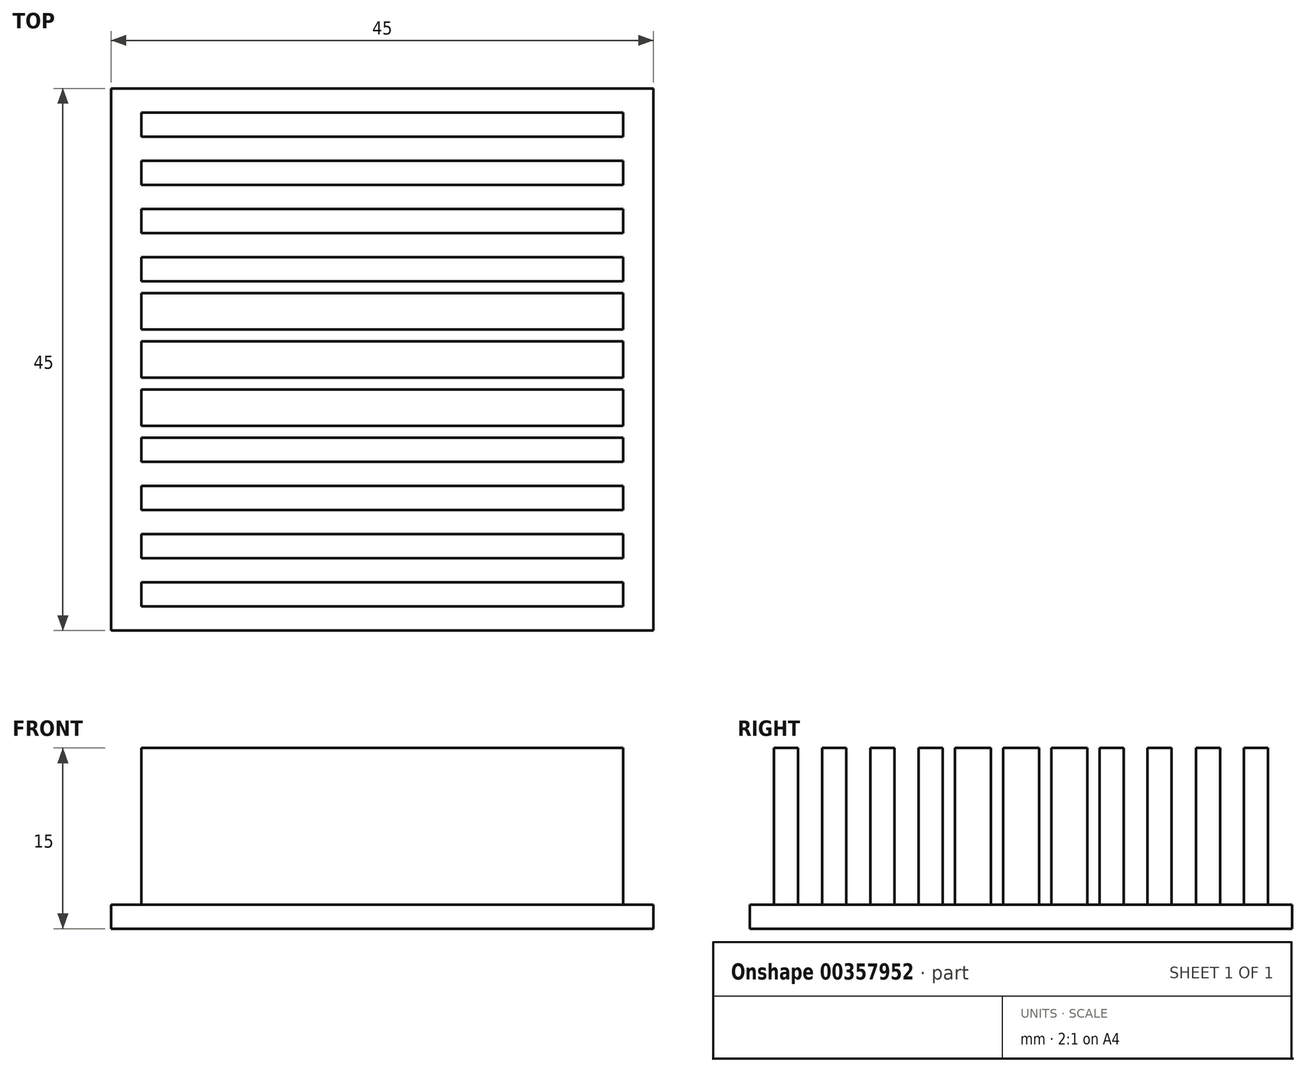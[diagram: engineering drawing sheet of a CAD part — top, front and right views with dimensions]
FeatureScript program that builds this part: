
annotation { "Feature Type Name" : "Feature", "Feature Type Description" : "" }
export const myFeature = defineFeature(function(context is Context, id is Id, definition is map)
    precondition{}
    {
        {
            var Q0;
            Q0=qCreatedBy(makeId("Top.planeOp"),FACE);
            var sketch = newSketch(context, id + "F0", { "sketchPlane" : qUnion([Q0])});
            skLineSegment(sketch, "E0.bottom", {"start": v(-22.5, 22.5) * mm, "end": v(22.5, 22.5) * mm});
            skLineSegment(sketch, "E0.top", {"start": v(-22.5, -22.5) * mm, "end": v(22.5, -22.5) * mm});
            skLineSegment(sketch, "E0.left", {"start": v(-22.5, 22.5) * mm, "end": v(-22.5, -22.5) * mm});
            skLineSegment(sketch, "E0.right", {"start": v(22.5, 22.5) * mm, "end": v(22.5, -22.5) * mm});
            skSolve(sketch);
        }
        {
            var Q0;
            Q0=qSketchRegion(id+"F0",true);
            extrude(context, id + "F1", {"entities" : qUnion([Q0]), "depth" : 15 * mm});
        }
        {
            var Q0;
            Q0=makeQuery(id+"F1.opExtrude","CAP_FACE",FACE,{"disambiguationData":[OSD([sQuery(id+"F0.wireOp",EDGE,"E0.bottom"),sQuery(id+"F0.wireOp",EDGE,"E0.top"),sQuery(id+"F0.wireOp",EDGE,"E0.left"),sQuery(id+"F0.wireOp",EDGE,"E0.right")])],"isStart":false});
            var sketch = newSketch(context, id + "F2", { "sketchPlane" : qUnion([Q0])});
            skLineSegment(sketch, "E1", {"start": v(-22.5, 22.5) * mm, "end": v(22.5, 22.5) * mm});
            skLineSegment(sketch, "E2", {"start": v(22.5, 22.5) * mm, "end": v(22.5, -22.5) * mm});
            skLineSegment(sketch, "E3", {"start": v(22.5, -22.5) * mm, "end": v(-22.5, -22.5) * mm});
            skLineSegment(sketch, "E4", {"start": v(-22.5, -22.5) * mm, "end": v(-22.5, 22.5) * mm});
            skLineSegment(sketch, "E5.bottom", {"start": v(-20, 20.5) * mm, "end": v(20, 20.5) * mm});
            skLineSegment(sketch, "E5.top", {"start": v(-20, 18.5) * mm, "end": v(20, 18.5) * mm});
            skLineSegment(sketch, "E5.left", {"start": v(-20, 20.5) * mm, "end": v(-20, 18.5) * mm});
            skLineSegment(sketch, "E5.right", {"start": v(20, 20.5) * mm, "end": v(20, 18.5) * mm});
            skLineSegment(sketch, "E6.bottom", {"start": v(-20, 16.5) * mm, "end": v(20, 16.5) * mm});
            skLineSegment(sketch, "E6.top", {"start": v(-20, 14.5) * mm, "end": v(20, 14.5) * mm});
            skLineSegment(sketch, "E6.left", {"start": v(-20, 16.5) * mm, "end": v(-20, 14.5) * mm});
            skLineSegment(sketch, "E6.right", {"start": v(20, 16.5) * mm, "end": v(20, 14.5) * mm});
            skLineSegment(sketch, "E7.bottom", {"start": v(-20, 12.5) * mm, "end": v(20, 12.5) * mm});
            skLineSegment(sketch, "E7.top", {"start": v(-20, 10.5) * mm, "end": v(20, 10.5) * mm});
            skLineSegment(sketch, "E7.left", {"start": v(-20, 12.5) * mm, "end": v(-20, 10.5) * mm});
            skLineSegment(sketch, "E7.right", {"start": v(20, 12.5) * mm, "end": v(20, 10.5) * mm});
            skLineSegment(sketch, "E8.bottom", {"start": v(-20, 8.5) * mm, "end": v(20, 8.5) * mm});
            skLineSegment(sketch, "E8.top", {"start": v(-20, 6.5) * mm, "end": v(20, 6.5) * mm});
            skLineSegment(sketch, "E8.left", {"start": v(-20, 8.5) * mm, "end": v(-20, 6.5) * mm});
            skLineSegment(sketch, "E8.right", {"start": v(20, 8.5) * mm, "end": v(20, 6.5) * mm});
            skLineSegment(sketch, "E9.bottom", {"start": v(-20, 4.5) * mm, "end": v(20, 4.5) * mm});
            skLineSegment(sketch, "E9.top", {"start": v(-20, 2.5) * mm, "end": v(20, 2.5) * mm});
            skLineSegment(sketch, "E9.left", {"start": v(-20, 4.5) * mm, "end": v(-20, 2.5) * mm});
            skLineSegment(sketch, "E9.right", {"start": v(20, 4.5) * mm, "end": v(20, 2.5) * mm});
            skLineSegment(sketch, "E10.bottom", {"start": v(-20, 0.5) * mm, "end": v(20, 0.5) * mm});
            skLineSegment(sketch, "E10.top", {"start": v(-20, -1.5) * mm, "end": v(20, -1.5) * mm});
            skLineSegment(sketch, "E10.left", {"start": v(-20, 0.5) * mm, "end": v(-20, -1.5) * mm});
            skLineSegment(sketch, "E10.right", {"start": v(20, 0.5) * mm, "end": v(20, -1.5) * mm});
            skLineSegment(sketch, "E11.bottom", {"start": v(-20, -3.5) * mm, "end": v(20, -3.5) * mm});
            skLineSegment(sketch, "E11.top", {"start": v(-20, -5.5) * mm, "end": v(20, -5.5) * mm});
            skLineSegment(sketch, "E11.left", {"start": v(-20, -3.5) * mm, "end": v(-20, -5.5) * mm});
            skLineSegment(sketch, "E11.right", {"start": v(20, -3.5) * mm, "end": v(20, -5.5) * mm});
            skLineSegment(sketch, "E12.MirrorCS", {"start": v(-20, -12.5) * mm, "end": v(-20, -10.5) * mm});
            skLineSegment(sketch, "E13.MirrorCS", {"start": v(20, -12.5) * mm, "end": v(20, -10.5) * mm});
            skLineSegment(sketch, "E14.MirrorCS", {"start": v(20, -0.5) * mm, "end": v(20, 1.5) * mm});
            skLineSegment(sketch, "E15.MirrorCS", {"start": v(20, -4.5) * mm, "end": v(20, -2.5) * mm});
            skLineSegment(sketch, "E16.MirrorCS", {"start": v(-20, -20.5) * mm, "end": v(-20, -18.5) * mm});
            skLineSegment(sketch, "E17.MirrorCS", {"start": v(20, -20.5) * mm, "end": v(20, -18.5) * mm});
            skLineSegment(sketch, "E18.MirrorCS", {"start": v(-20, -16.5) * mm, "end": v(-20, -14.5) * mm});
            skLineSegment(sketch, "E19.MirrorCS", {"start": v(20, -16.5) * mm, "end": v(20, -14.5) * mm});
            skLineSegment(sketch, "E20.MirrorCS", {"start": v(20, -8.5) * mm, "end": v(20, -6.5) * mm});
            skLineSegment(sketch, "E21.MirrorCS", {"start": v(-20, -0.5) * mm, "end": v(-20, 1.5) * mm});
            skLineSegment(sketch, "E22.MirrorCS", {"start": v(-20, -4.5) * mm, "end": v(-20, -2.5) * mm});
            skLineSegment(sketch, "E23.MirrorCS", {"start": v(20, 3.5) * mm, "end": v(20, 5.5) * mm});
            skLineSegment(sketch, "E24.MirrorCS", {"start": v(-20, 3.5) * mm, "end": v(-20, 5.5) * mm});
            skLineSegment(sketch, "E25.MirrorCS", {"start": v(-20, -8.5) * mm, "end": v(-20, -6.5) * mm});
            skLineSegment(sketch, "E26.MirrorCS", {"start": v(-20, -10.5) * mm, "end": v(20, -10.5) * mm});
            skLineSegment(sketch, "E27.MirrorCS", {"start": v(-20, -20.5) * mm, "end": v(20, -20.5) * mm});
            skLineSegment(sketch, "E28.MirrorCS", {"start": v(-20, -6.5) * mm, "end": v(20, -6.5) * mm});
            skLineSegment(sketch, "E29.MirrorCS", {"start": v(-20, -18.5) * mm, "end": v(20, -18.5) * mm});
            skLineSegment(sketch, "E30.MirrorCS", {"start": v(-20, 5.5) * mm, "end": v(20, 5.5) * mm});
            skLineSegment(sketch, "E31.MirrorCS", {"start": v(-20, -4.5) * mm, "end": v(20, -4.5) * mm});
            skLineSegment(sketch, "E32.MirrorCS", {"start": v(-20, -16.5) * mm, "end": v(20, -16.5) * mm});
            skLineSegment(sketch, "E33.MirrorCS", {"start": v(-20, -14.5) * mm, "end": v(20, -14.5) * mm});
            skLineSegment(sketch, "E34.MirrorCS", {"start": v(-20, -8.5) * mm, "end": v(20, -8.5) * mm});
            skLineSegment(sketch, "E35.MirrorCS", {"start": v(-20, 3.5) * mm, "end": v(20, 3.5) * mm});
            skLineSegment(sketch, "E36.MirrorCS", {"start": v(-20, -0.5) * mm, "end": v(20, -0.5) * mm});
            skLineSegment(sketch, "E37.MirrorCS", {"start": v(-20, -12.5) * mm, "end": v(20, -12.5) * mm});
            skLineSegment(sketch, "E38.MirrorCS", {"start": v(-20, 1.5) * mm, "end": v(20, 1.5) * mm});
            skLineSegment(sketch, "E39.MirrorCS", {"start": v(-20, -2.5) * mm, "end": v(20, -2.5) * mm});
            skSolve(sketch);
        }
        {
            var Q0;
            Q0=qSketchRegion(id+"F2",true);
            extrude(context, id + "F3", {"entities" : qUnion([Q0]), "operationType" : NewBodyOperationType.REMOVE, "oppositeDirection" : true, "depth" : 13 * mm});
        }
    });
